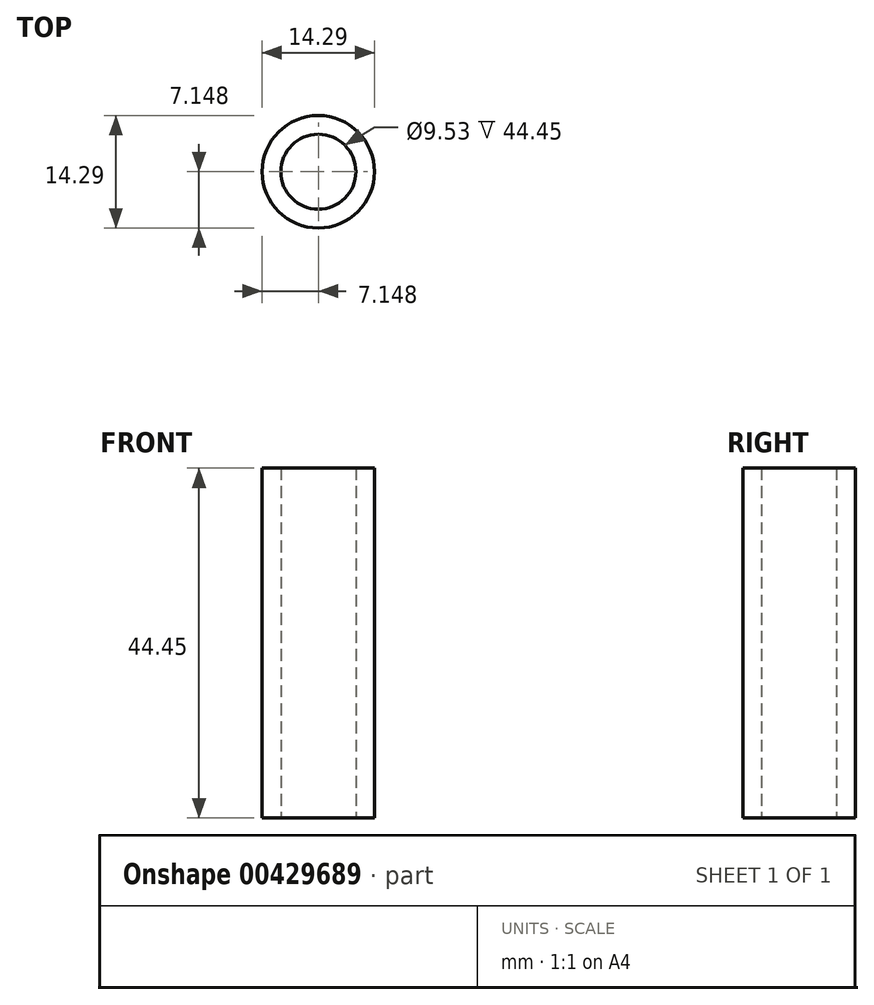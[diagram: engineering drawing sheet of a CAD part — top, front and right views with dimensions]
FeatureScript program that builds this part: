
annotation { "Feature Type Name" : "Feature", "Feature Type Description" : "" }
export const myFeature = defineFeature(function(context is Context, id is Id, definition is map)
    precondition{}
    {
        {
            var Q0;
            Q0=qCreatedBy(makeId("Top.planeOp"),FACE);
            var sketch = newSketch(context, id + "F0", { "sketchPlane" : qUnion([Q0])});
            skCircle(sketch, "E0", {"center": v(-46.77, -40.6) * mm, "radius": 7.14 * mm});
            skCircle(sketch, "E1", {"center": v(-46.77, -40.6) * mm, "radius": 4.76 * mm});
            skSolve(sketch);
        }
        {
            var Q0;
            Q0=makeQuery(id+"F0.imprint","IMPRINT",FACE,{"disambiguationData":[TD([[makeQuery(id+"F0.imprint","IMPRINT",EDGE,{"derivedFrom":sQuery(id+"F0.wireOp",EDGE,"E0")}),1.0]])]});
            extrude(context, id + "F1", {"entities" : qUnion([Q0]), "depth" : 44.45 * mm});
        }
    });
